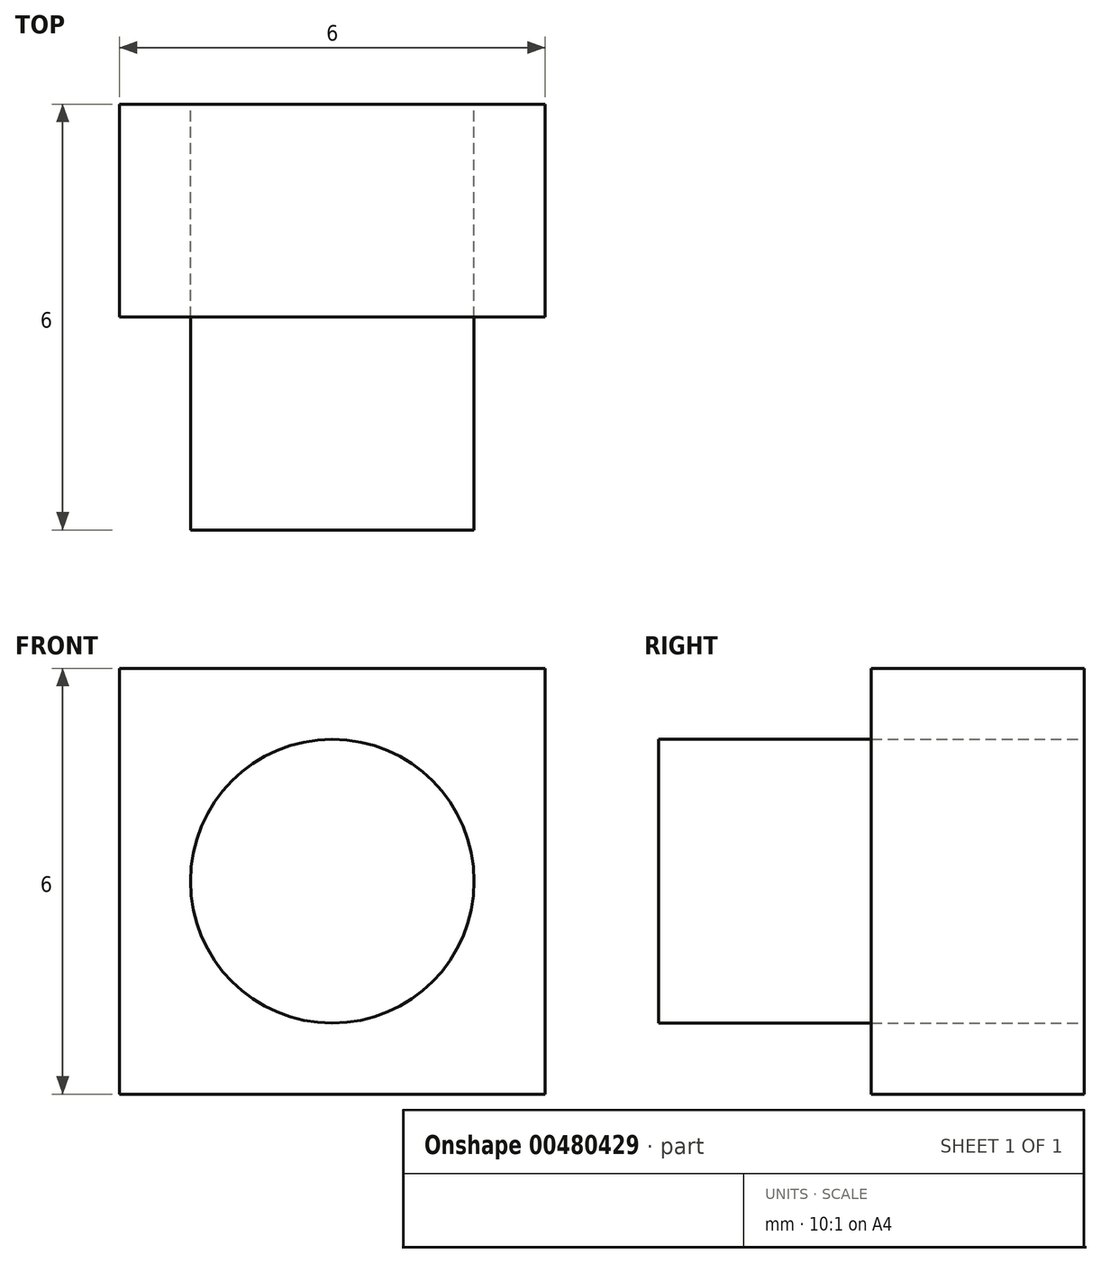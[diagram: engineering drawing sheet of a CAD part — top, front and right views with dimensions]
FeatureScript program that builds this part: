
annotation { "Feature Type Name" : "Feature", "Feature Type Description" : "" }
export const myFeature = defineFeature(function(context is Context, id is Id, definition is map)
    precondition{}
    {
        {
            var Q0;
            Q0=qCreatedBy(makeId("Front.planeOp"),FACE);
            var sketch = newSketch(context, id + "F0", { "sketchPlane" : qUnion([Q0])});
            skLineSegment(sketch, "E0.bottom", {"start": v(0, 0) * mm, "end": v(-6, 0) * mm});
            skLineSegment(sketch, "E0.top", {"start": v(0, 6) * mm, "end": v(-6, 6) * mm});
            skLineSegment(sketch, "E0.left", {"start": v(0, 0) * mm, "end": v(0, 6) * mm});
            skLineSegment(sketch, "E0.right", {"start": v(-6, 0) * mm, "end": v(-6, 6) * mm});
            skCircle(sketch, "E1", {"center": v(-3, 3) * mm, "radius": 2 * mm});
            skPoint(sketch, "E1.centerSnap0", {"position": v(0, 3) * mm});
            skPoint(sketch, "E1.centerSnap1", {"position": v(-3, 0) * mm});
            skSolve(sketch);
        }
        {
            var Q0;
            Q0=makeQuery(id+"F0.imprint","IMPRINT",FACE,{"disambiguationData":[TD([[makeQuery(id+"F0.imprint","IMPRINT",EDGE,{"derivedFrom":sQuery(id+"F0.wireOp",EDGE,"E1")}),1.0]])]});
            extrude(context, id + "F1", {"entities" : qUnion([Q0]), "depth" : 6 * mm});
        }
        {
            var Q0;
            Q0=makeQuery(id+"F0.imprint","IMPRINT",FACE,{"disambiguationData":[TD([[makeQuery(id+"F0.imprint","IMPRINT",EDGE,{"derivedFrom":sQuery(id+"F0.wireOp",EDGE,"E0.bottom")}),-1.0]])]});
            extrude(context, id + "F2", {"entities" : qUnion([Q0]), "depth" : 3 * mm});
        }
    });
